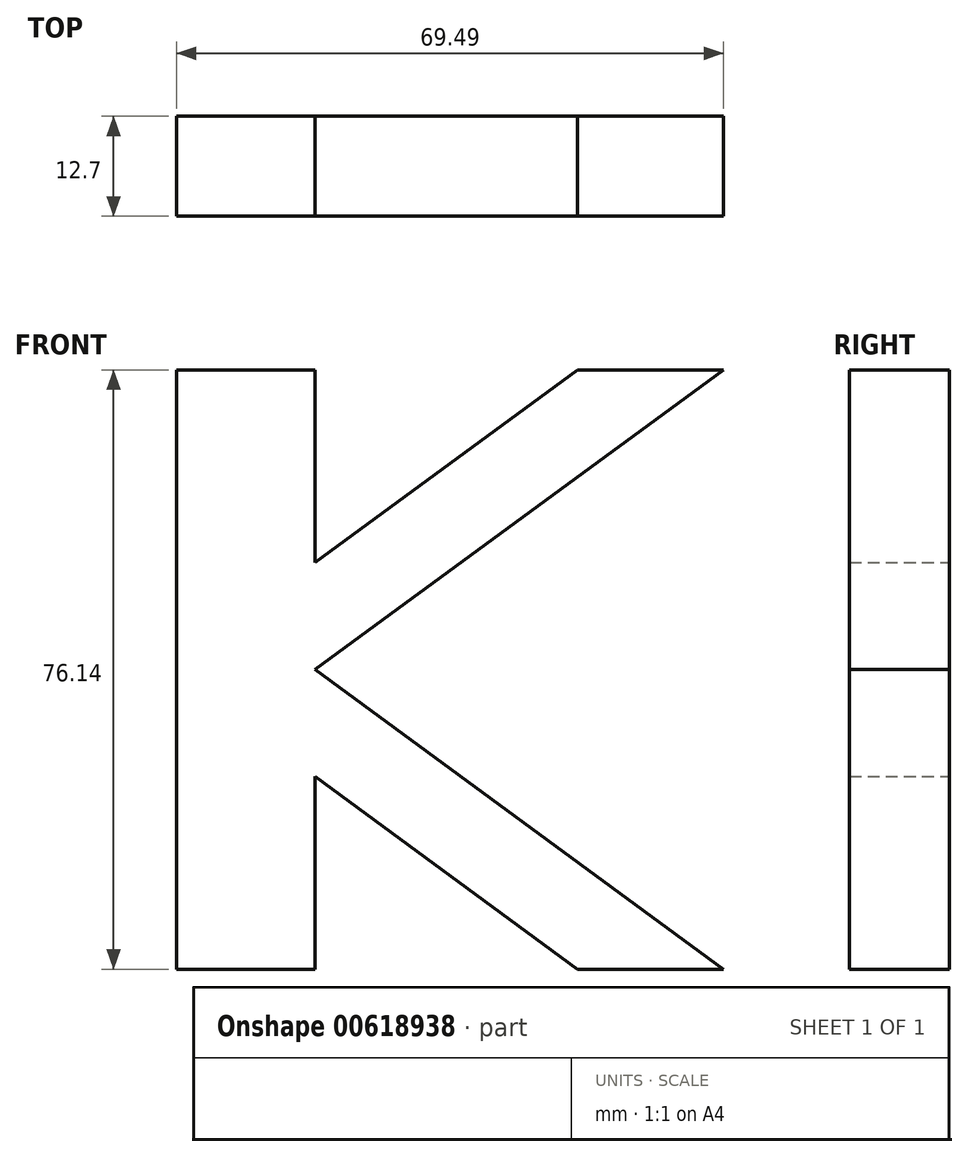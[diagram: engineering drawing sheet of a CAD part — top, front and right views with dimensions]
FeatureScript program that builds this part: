
annotation { "Feature Type Name" : "Feature", "Feature Type Description" : "" }
export const myFeature = defineFeature(function(context is Context, id is Id, definition is map)
    precondition{}
    {
        {
            var Q0;
            Q0=qCreatedBy(makeId("Front.planeOp"),FACE);
            var sketch = newSketch(context, id + "F0", { "sketchPlane" : qUnion([Q0])});
            skLineSegment(sketch, "E0.bottom", {"start": v(-17.58, 0) * mm, "end": v(0, 0) * mm});
            skLineSegment(sketch, "E0.top", {"start": v(-17.58, 76.14) * mm, "end": v(0, 76.14) * mm});
            skLineSegment(sketch, "E0.right", {"start": v(0, 0) * mm, "end": v(0, 76.14) * mm});
            skLineSegment(sketch, "E1", {"start": v(0, 51.68) * mm, "end": v(33.35, 76.14) * mm});
            skLineSegment(sketch, "E2", {"start": v(33.35, 76.14) * mm, "end": v(51.9, 76.14) * mm});
            skLineSegment(sketch, "E3", {"start": v(51.9, 76.14) * mm, "end": v(0, 38.07) * mm});
            skLineSegment(sketch, "E4", {"start": v(0, 38.07) * mm, "end": v(51.9, 0) * mm});
            skLineSegment(sketch, "E5", {"start": v(0, 24.46) * mm, "end": v(33.35, 0) * mm});
            skLineSegment(sketch, "E6", {"start": v(33.35, 0) * mm, "end": v(51.9, 0) * mm});
            skLineSegment(sketch, "E7", {"start": v(0, 51.68) * mm, "end": v(0, 38.07) * mm, "construction": true});
            skLineSegment(sketch, "E8", {"start": v(0, 38.07) * mm, "end": v(0, 24.46) * mm, "construction": true});
            skPoint(sketch, "E9", {"position": v(-17.58, 38.07) * mm});
            skLineSegment(sketch, "E10", {"start": v(-17.58, 76.14) * mm, "end": v(-17.58, 0) * mm});
            skSolve(sketch);
        }
        {
            var Q0;
            Q0 = qSketchRegion(id + "F0", true);
            extrude(context, id + "F1", {"entities" : qUnion([Q0]), "depth" : 12.7 * mm, "offsetDistance" : 25.4 * mm});
        }
    });
